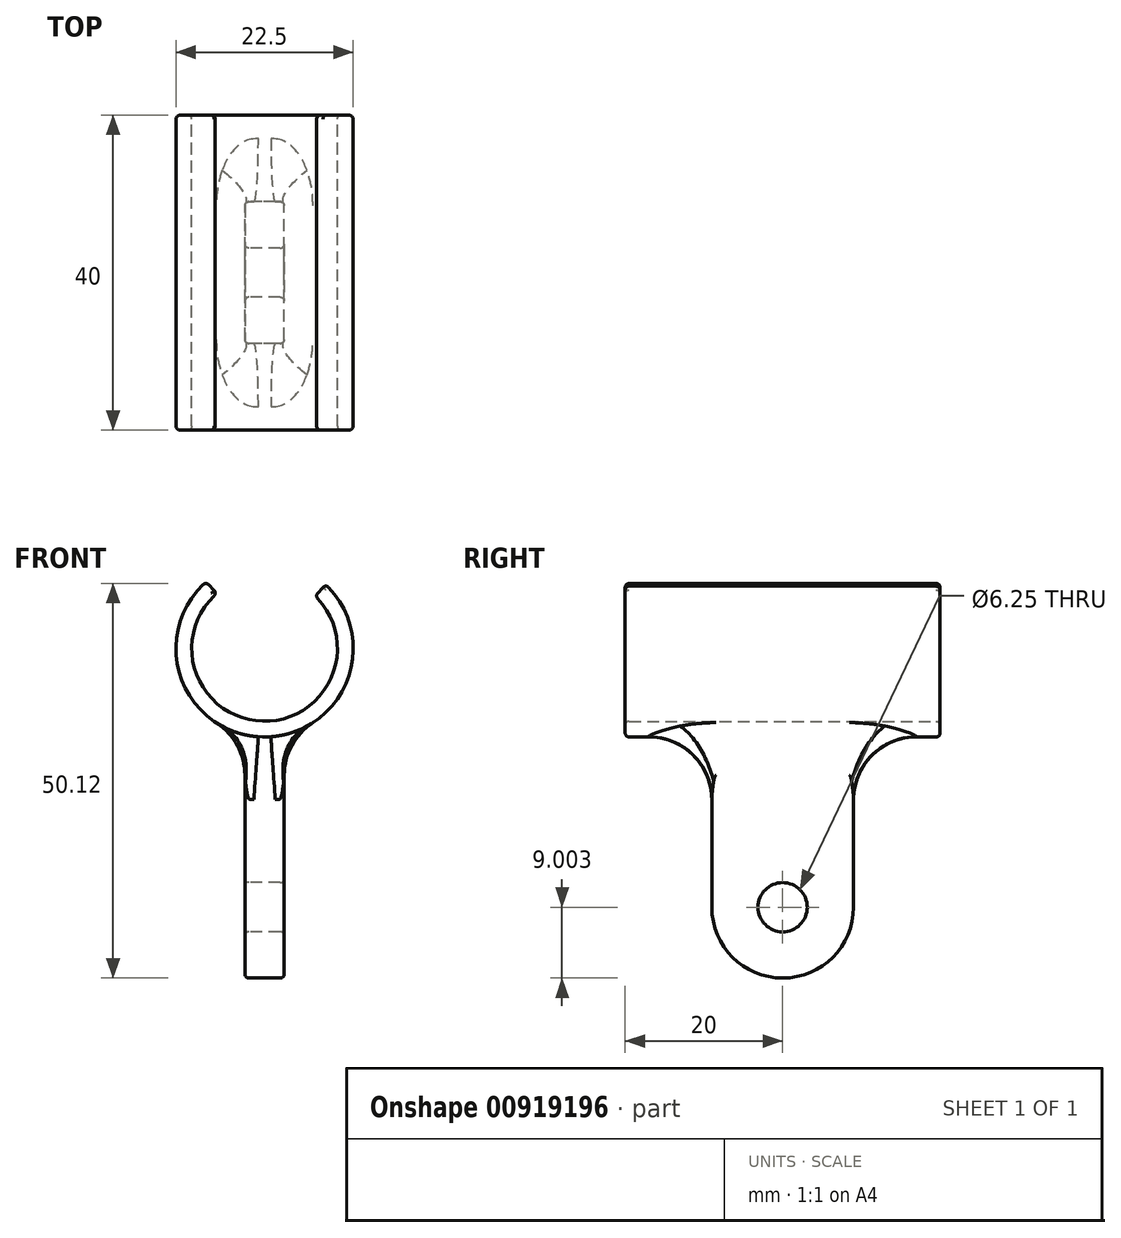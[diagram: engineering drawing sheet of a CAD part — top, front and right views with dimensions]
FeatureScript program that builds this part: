
annotation { "Feature Type Name" : "Feature", "Feature Type Description" : "" }
export const myFeature = defineFeature(function(context is Context, id is Id, definition is map)
    precondition{}
    {
        {
            var Q0;
            Q0=qCreatedBy(makeId("Front.planeOp"),FACE);
            var sketch = newSketch(context, id + "F0", { "sketchPlane" : qUnion([Q0])});
            skArc(sketch, "E0", {"start": v(-6.05, 7) * mm, "mid": v(-0.26, -9.25) * mm, "end": v(6.43, 6.65) * mm});
            skArc(sketch, "E1", {"start": v(-7.43, 8.45) * mm, "mid": v(-0.23, -11.25) * mm, "end": v(7.77, 8.13) * mm});
            skLineSegment(sketch, "E2", {"start": v(-7.43, 8.45) * mm, "end": v(-6.05, 7) * mm});
            skLineSegment(sketch, "E3", {"start": v(6.43, 6.65) * mm, "end": v(7.77, 8.13) * mm});
            skSolve(sketch);
        }
        {
            var Q0;
            Q0=makeQuery(id+"F0.imprint","IMPRINT",FACE,{"disambiguationData":[TD([[makeQuery(id+"F0.imprint","IMPRINT",EDGE,{"derivedFrom":sQuery(id+"F0.wireOp",EDGE,"E0")}),-1.0]])]});
            extrude(context, id + "F1", {"entities" : qUnion([Q0]), "depth" : 40 * mm, "offsetDistance" : 25 * mm, "symmetric" : true});
        }
        {
            var Q0;
            Q0=qCreatedBy(makeId("Right.planeOp"),FACE);
            var sketch = newSketch(context, id + "F2", { "sketchPlane" : qUnion([Q0])});
            skLineSegment(sketch, "E4.bottom", {"start": v(-9, -9.88) * mm, "end": v(9, -9.88) * mm});
            skLineSegment(sketch, "E4.top", {"start": v(-9, -32.88) * mm, "end": v(9, -32.88) * mm});
            skLineSegment(sketch, "E4.left", {"start": v(-9, -9.88) * mm, "end": v(-9, -32.88) * mm});
            skLineSegment(sketch, "E4.right", {"start": v(9, -9.88) * mm, "end": v(9, -32.88) * mm});
            skArc(sketch, "E5", {"start": v(-9, -32.88) * mm, "mid": v(0, -41.88) * mm, "end": v(9, -32.88) * mm});
            skCircle(sketch, "E6", {"center": v(0, -32.88) * mm, "radius": 3.12 * mm});
            skSolve(sketch);
        }
        {
            var Q0;
            Q0=makeQuery(id+"F2.imprint","IMPRINT",FACE,{"disambiguationData":[TD([[makeQuery(id+"F2.imprint","IMPRINT",EDGE,{"derivedFrom":sQuery(id+"F2.wireOp",EDGE,"E4.bottom")}),-1.0]])]});
            var Q1;
            Q1=makeQuery(id+"F2.imprint","IMPRINT",FACE,{"disambiguationData":[TD([[makeQuery(id+"F2.imprint","IMPRINT",EDGE,{"derivedFrom":sQuery(id+"F2.wireOp",EDGE,"E4.top")}),-1.0]])]});
            extrude(context, id + "F3", {"entities" : qUnion([Q0, Q1]), "operationType" : NewBodyOperationType.ADD, "depth" : 5 * mm, "offsetDistance" : 25 * mm, "symmetric" : true});
        }
        {
            var Q0;
            Q0=makeQuery(id+"F3.opExtrude","CAP_EDGE",EDGE,{"disambiguationData":[OSD([sQuery(id+"F2.wireOp",EDGE,"E4.right")])],"isStart":true});
            var Q1;
            Q1=makeQuery(id+"F3.opExtrude","CAP_EDGE",EDGE,{"disambiguationData":[OSD([sQuery(id+"F2.wireOp",EDGE,"E4.right")])],"isStart":false});
            var Q2;
            Q2=makeQuery(id+"F1.opExtrude","SWEPT_EDGE",EDGE,{"disambiguationData":[OSD([sQuery(id+"F0.wireOp",EDGE,"E1"),sQuery(id+"F0.wireOp",EDGE,"E2")])]});
            var Q3;
            Q3=makeQuery(id+"F1.opExtrude","CAP_EDGE",EDGE,{"disambiguationData":[OSD([sQuery(id+"F0.wireOp",EDGE,"E1")])],"isStart":true});
            var Q4;
            Q4=makeQuery(id+"F1.opExtrude","CAP_EDGE",EDGE,{"disambiguationData":[OSD([sQuery(id+"F0.wireOp",EDGE,"E0")])],"isStart":true});
            var Q5;
            Q5=makeQuery(id+"F1.opExtrude","CAP_EDGE",EDGE,{"disambiguationData":[OSD([sQuery(id+"F0.wireOp",EDGE,"E1")])],"isStart":false});
            var Q6;
            Q6=makeQuery(id+"F1.opExtrude","CAP_EDGE",EDGE,{"disambiguationData":[OSD([sQuery(id+"F0.wireOp",EDGE,"E0")])],"isStart":false});
            var Q7;
            Q7=makeQuery(id+"F1.opExtrude","SWEPT_EDGE",EDGE,{"disambiguationData":[OSD([sQuery(id+"F0.wireOp",EDGE,"E1"),sQuery(id+"F0.wireOp",EDGE,"E3")])]});
            var Q8;
            Q8=makeQuery(id+"F1.opExtrude","SWEPT_EDGE",EDGE,{"disambiguationData":[OSD([sQuery(id+"F0.wireOp",EDGE,"E0"),sQuery(id+"F0.wireOp",EDGE,"E3")])]});
            var Q9;
            Q9=makeQuery(id+"F1.opExtrude","SWEPT_EDGE",EDGE,{"disambiguationData":[OSD([sQuery(id+"F0.wireOp",EDGE,"E0"),sQuery(id+"F0.wireOp",EDGE,"E2")])]});
            var Q10;
            Q10=makeQuery(id+"F3.opExtrude","CAP_EDGE",EDGE,{"disambiguationData":[OSD([sQuery(id+"F2.wireOp",EDGE,"E6")])],"isStart":false});
            var Q11;
            Q11=makeQuery(id+"F3.opExtrude","CAP_EDGE",EDGE,{"disambiguationData":[OSD([sQuery(id+"F2.wireOp",EDGE,"E6")])],"isStart":true});
            var Q12;
            Q12=makeQuery(id+"F1.opExtrude","CAP_EDGE",EDGE,{"disambiguationData":[OSD([sQuery(id+"F0.wireOp",EDGE,"E3")])],"isStart":false});
            var Q13;
            Q13=makeQuery(id+"F1.opExtrude","CAP_EDGE",EDGE,{"disambiguationData":[OSD([sQuery(id+"F0.wireOp",EDGE,"E2")])],"isStart":false});
            var Q14;
            Q14=makeQuery(id+"F1.opExtrude","CAP_EDGE",EDGE,{"disambiguationData":[OSD([sQuery(id+"F0.wireOp",EDGE,"E2")])],"isStart":true});
            var Q15;
            Q15=makeQuery(id+"F1.opExtrude","CAP_EDGE",EDGE,{"disambiguationData":[OSD([sQuery(id+"F0.wireOp",EDGE,"E3")])],"isStart":true});
            fillet(context, id + "F4", {"entities" : qUnion([Q0, Q1, Q2, Q3, Q4, Q5, Q6, Q7, Q8, Q9, Q10, Q11, Q12, Q13, Q14, Q15]), "radius" : 0.5 * mm, "tangentPropagation" : true, "allowEdgeOverflow" : false});
        }
        {
            var Q0;
            Q0=makeQuery(id+"F3.opExtrude","CAP_EDGE",EDGE,{"disambiguationData":[OSD([sQuery(id+"F2.wireOp",EDGE,"E4.bottom")])],"isStart":true});
            var Q1;
            Q1=makeQuery(id+"F3.opExtrude","CAP_EDGE",EDGE,{"disambiguationData":[OSD([sQuery(id+"F2.wireOp",EDGE,"E4.bottom")])],"isStart":false});
            var Q2;
            Q2=makeQuery(id+"F3.boolean.opBoolean","INTERSECT",EDGE,{"derivedFrom":[makeQuery(id+"F1.opExtrude","SWEPT_FACE",FACE,{"disambiguationData":[OSD([sQuery(id+"F0.wireOp",EDGE,"E1")])]}),makeQuery(id+"F3.opExtrude","SWEPT_FACE",FACE,{"disambiguationData":[OSD([sQuery(id+"F2.wireOp",EDGE,"E4.right")])]})]});
            fillet(context, id + "F5", {"entities" : qUnion([Q0, Q1, Q2]), "radius" : 8 * mm, "tangentPropagation" : true, "allowEdgeOverflow" : false});
        }
    });
